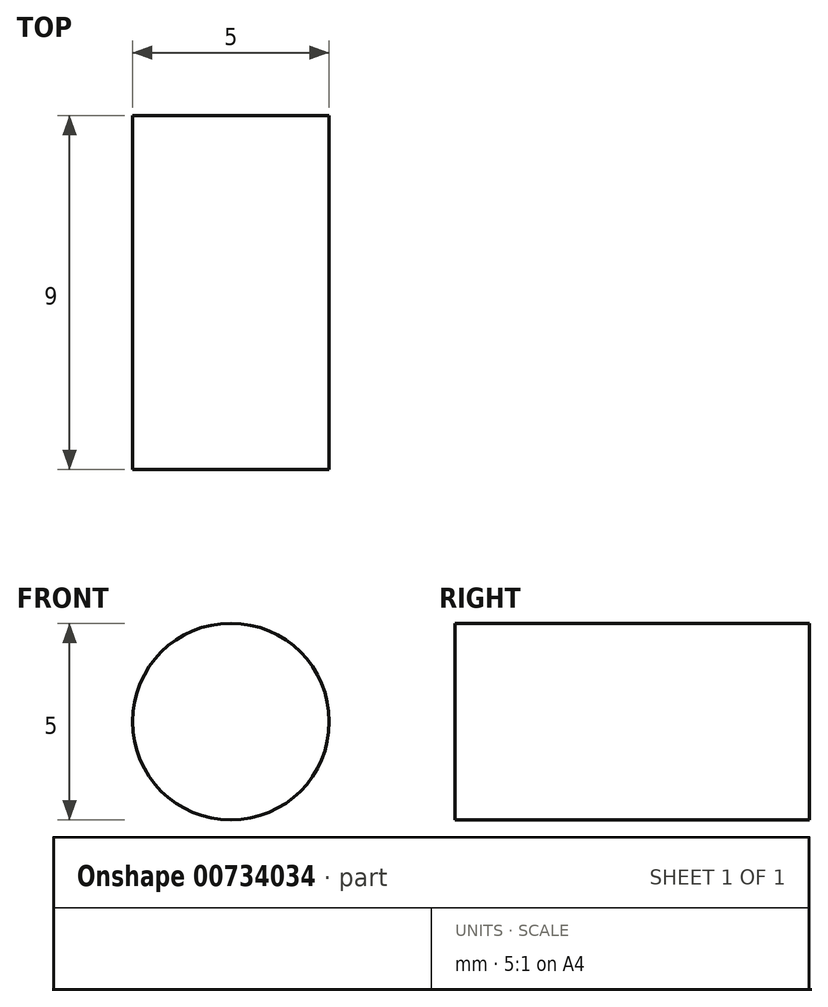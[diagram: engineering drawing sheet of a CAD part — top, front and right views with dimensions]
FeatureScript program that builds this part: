
annotation { "Feature Type Name" : "Feature", "Feature Type Description" : "" }
export const myFeature = defineFeature(function(context is Context, id is Id, definition is map)
    precondition{}
    {
        {
            var Q0;
            Q0=qCreatedBy(makeId("Front.planeOp"),FACE);
            var sketch = newSketch(context, id + "F0", { "sketchPlane" : qUnion([Q0])});
            skCircle(sketch, "E0", {"center": v(0, 0) * mm, "radius": 2.5 * mm});
            skSolve(sketch);
        }
        {
            var Q0;
            Q0=qSketchRegion(id+"F0",true);
            extrude(context, id + "F1", {"entities" : qUnion([Q0]), "depth" : 9 * mm, "offsetDistance" : 25 * mm});
        }
    });
